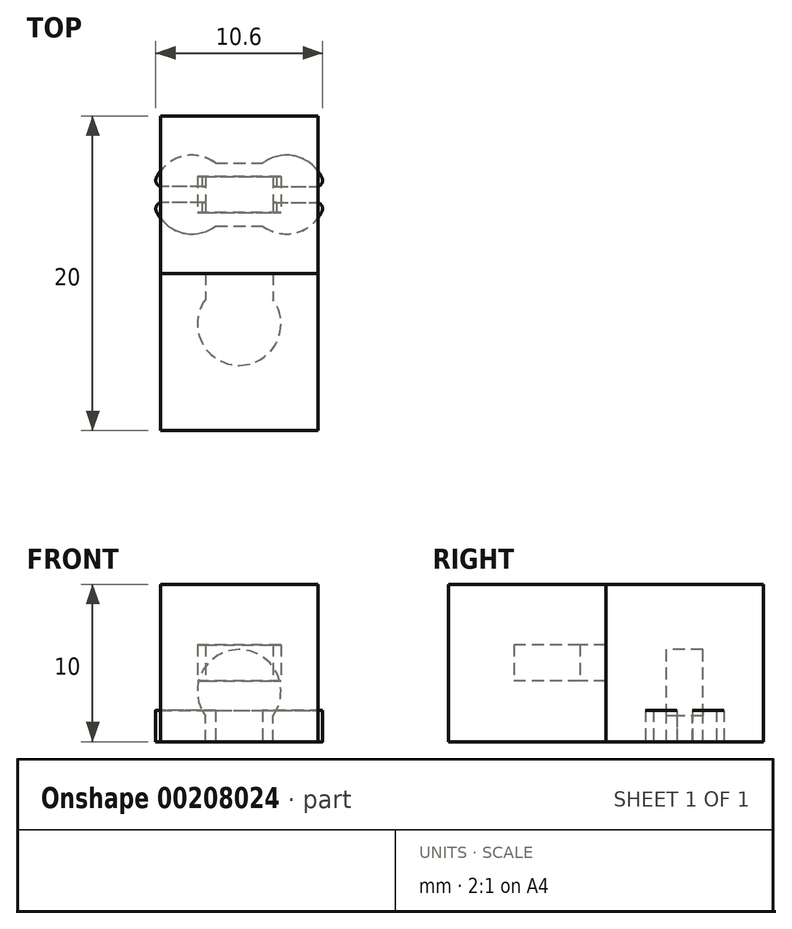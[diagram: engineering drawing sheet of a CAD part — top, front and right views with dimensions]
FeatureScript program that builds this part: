
annotation { "Feature Type Name" : "Feature", "Feature Type Description" : "" }
export const myFeature = defineFeature(function(context is Context, id is Id, definition is map)
    precondition{}
    {
        {
            var Q0;
            Q0=qCreatedBy(makeId("Top.planeOp"),FACE);
            var sketch = newSketch(context, id + "F0", { "sketchPlane" : qUnion([Q0])});
            skArc(sketch, "E0", {"start": v(-5.26, -1.07) * mm, "mid": v(-3.6, -2.43) * mm, "end": v(-1.5, -2) * mm});
            skLineSegment(sketch, "E1", {"start": v(0, 0) * mm, "end": v(0, 6.78) * mm, "construction": true});
            skLineSegment(sketch, "E2", {"start": v(0, 0) * mm, "end": v(-9.78, 0) * mm, "construction": true});
            skLineSegment(sketch, "E3", {"start": v(-1.5, 2) * mm, "end": v(0, 2) * mm});
            skLineSegment(sketch, "E4.MirrorCS", {"start": v(-1.5, -2) * mm, "end": v(0, -2) * mm});
            skLineSegment(sketch, "E5.bottom", {"start": v(-1.5, 0.5) * mm, "end": v(-4.9, 0.5) * mm});
            skLineSegment(sketch, "E5.top", {"start": v(-1.5, -0.5) * mm, "end": v(-4.9, -0.5) * mm});
            skLineSegment(sketch, "E5.left", {"start": v(-1.5, 0.5) * mm, "end": v(-1.5, -0.5) * mm, "construction": true});
            skArc(sketch, "E6", {"start": v(-1.5, -0.5) * mm, "mid": v(-1, 0) * mm, "end": v(-1.5, 0.5) * mm});
            skArc(sketch, "E7", {"start": v(-5.26, 1.07) * mm, "mid": v(-5.24, 0.69) * mm, "end": v(-4.9, 0.5) * mm});
            skArc(sketch, "E8.MirrorCS", {"start": v(-5.26, -1.07) * mm, "mid": v(-5.24, -0.69) * mm, "end": v(-4.9, -0.5) * mm});
            skArc(sketch, "E9.trimOffspring", {"start": v(-1.5, 2) * mm, "mid": v(-3.6, 2.43) * mm, "end": v(-5.26, 1.07) * mm});
            skLineSegment(sketch, "E10.MirrorCS", {"start": v(1.5, -2) * mm, "end": v(0, -2) * mm});
            skLineSegment(sketch, "E11.MirrorCS", {"start": v(1.5, 0.5) * mm, "end": v(4.9, 0.5) * mm});
            skLineSegment(sketch, "E12.MirrorCS", {"start": v(1.5, 0.5) * mm, "end": v(1.5, -0.5) * mm, "construction": true});
            skLineSegment(sketch, "E13.MirrorCS", {"start": v(1.5, -0.5) * mm, "end": v(4.9, -0.5) * mm});
            skArc(sketch, "E14.MirrorCS", {"start": v(5.26, 1.07) * mm, "mid": v(5.24, 0.69) * mm, "end": v(4.9, 0.5) * mm});
            skArc(sketch, "E15.MirrorCS", {"start": v(1.5, -0.5) * mm, "mid": v(1, 0) * mm, "end": v(1.5, 0.5) * mm});
            skArc(sketch, "E16.MirrorCS", {"start": v(1.5, 2) * mm, "mid": v(3.6, 2.43) * mm, "end": v(5.26, 1.07) * mm});
            skArc(sketch, "E17.MirrorCS", {"start": v(5.26, -1.07) * mm, "mid": v(5.24, -0.69) * mm, "end": v(4.9, -0.5) * mm});
            skLineSegment(sketch, "E18.MirrorCS", {"start": v(1.5, 2) * mm, "end": v(0, 2) * mm});
            skArc(sketch, "E19.MirrorCS", {"start": v(5.26, -1.07) * mm, "mid": v(3.6, -2.43) * mm, "end": v(1.5, -2) * mm});
            skSolve(sketch);
        }
        {
            var Q0;
            Q0=makeQuery(id+"F0.imprint","IMPRINT",FACE,{"disambiguationData":[TD([[makeQuery(id+"F0.imprint","IMPRINT",EDGE,{"derivedFrom":sQuery(id+"F0.wireOp",EDGE,"E0")}),1.0]])]});
            extrude(context, id + "F1", {"entities" : qUnion([Q0]), "depth" : 2 * mm});
        }
        {
            var Q0;
            Q0=qCreatedBy(makeId("Top.planeOp"),FACE);
            var sketch = newSketch(context, id + "F2", { "sketchPlane" : qUnion([Q0])});
            skLineSegment(sketch, "E20.bottom", {"start": v(5, 5) * mm, "end": v(-5, 5) * mm});
            skLineSegment(sketch, "E20.top", {"start": v(5, -5) * mm, "end": v(-5, -5) * mm});
            skLineSegment(sketch, "E20.left", {"start": v(5, 5) * mm, "end": v(5, -5) * mm});
            skLineSegment(sketch, "E20.right", {"start": v(-5, 5) * mm, "end": v(-5, -5) * mm});
            skPoint(sketch, "E20.middle", {"position": v(0, 0) * mm});
            skSolve(sketch);
        }
        {
            var Q0;
            {var subQ0=sQuery(id+"F2.wireOp",EDGE,"E20.right");Q0=makeQuery(id+"F2.imprint","IMPRINT",FACE,{"disambiguationData":[TD([[makeQuery(id+"F2.imprint","IMPRINT",EDGE,{"derivedFrom":subQ0}),1.0]])]});}
            extrude(context, id + "F3", {"entities" : qUnion([Q0]), "depth" : 10 * mm});
        }
        {
            var Q0;
            Q0=qCreatedBy(makeId("Front.planeOp"),FACE);
            var sketch = newSketch(context, id + "F4", { "sketchPlane" : qUnion([Q0])});
            skLineSegment(sketch, "E21", {"start": v(0, 0) * mm, "end": v(0, 3.2) * mm, "construction": true});
            skLineSegment(sketch, "E22.bottom", {"start": v(-2.15, 0) * mm, "end": v(2.15, 0) * mm});
            skLineSegment(sketch, "E22.top", {"start": v(-2.15, 2.13) * mm, "end": v(2.15, 2.13) * mm});
            skLineSegment(sketch, "E22.left", {"start": v(-2.15, 0) * mm, "end": v(-2.15, 2.13) * mm});
            skLineSegment(sketch, "E22.right", {"start": v(2.15, 0) * mm, "end": v(2.15, 2.13) * mm});
            skPoint(sketch, "E22.middle", {"position": v(0, 1.06) * mm});
            skCircle(sketch, "E23", {"center": v(0, 3.2) * mm, "radius": 2.65 * mm});
            skSolve(sketch);
        }
        {
            var Q0;
            {var subQ5=sQuery(id+"F4.wireOp",EDGE,"E22.bottom");Q0=makeQuery(id+"F4.imprint","IMPRINT",FACE,{"disambiguationData":[TD([[makeQuery(id+"F4.imprint","IMPRINT",EDGE,{"derivedFrom":subQ5}),1.0]])]});}
            var Q1;
            {var subQ5=sQuery(id+"F4.wireOp",EDGE,"E22.top");Q1=makeQuery(id+"F4.imprint","IMPRINT",FACE,{"disambiguationData":[TD([[makeQuery(id+"F4.imprint","IMPRINT",EDGE,{"derivedFrom":subQ5}),-1.0]])]});}
            var Q2;
            {var subQ5=sQuery(id+"F4.wireOp",EDGE,"E22.top");Q2=makeQuery(id+"F4.imprint","IMPRINT",FACE,{"disambiguationData":[TD([[makeQuery(id+"F4.imprint","IMPRINT",EDGE,{"derivedFrom":subQ5}),1.0]])]});}
            extrude(context, id + "F5", {"entities" : qUnion([Q0, Q1, Q2]), "operationType" : NewBodyOperationType.REMOVE, "oppositeDirection" : true, "depth" : 2.3 * mm, "symmetric" : true});
        }
        {
            var Q0;
            Q0=makeQuery(id+"F3.opExtrude","SWEPT_BODY",BODY,{"disambiguationData":[OSD([sQuery(id+"F2.wireOp",EDGE,"E20.bottom"),sQuery(id+"F2.wireOp",EDGE,"E20.top"),sQuery(id+"F2.wireOp",EDGE,"E20.left"),sQuery(id+"F2.wireOp",EDGE,"E20.right")])]});
            var Q1;
            Q1=makeQuery(id+"F3.opExtrude","CAP_EDGE",EDGE,{"disambiguationData":[OSD([sQuery(id+"F2.wireOp",EDGE,"E20.top")])],"isStart":true});
            circularPattern(context, id + "F6", {"entities" : qUnion([Q0]), "axis" : qUnion([Q1]), "angle" : 90 * degree, "instanceCount" : 2, "oppositeDirection" : true});
        }
    });
